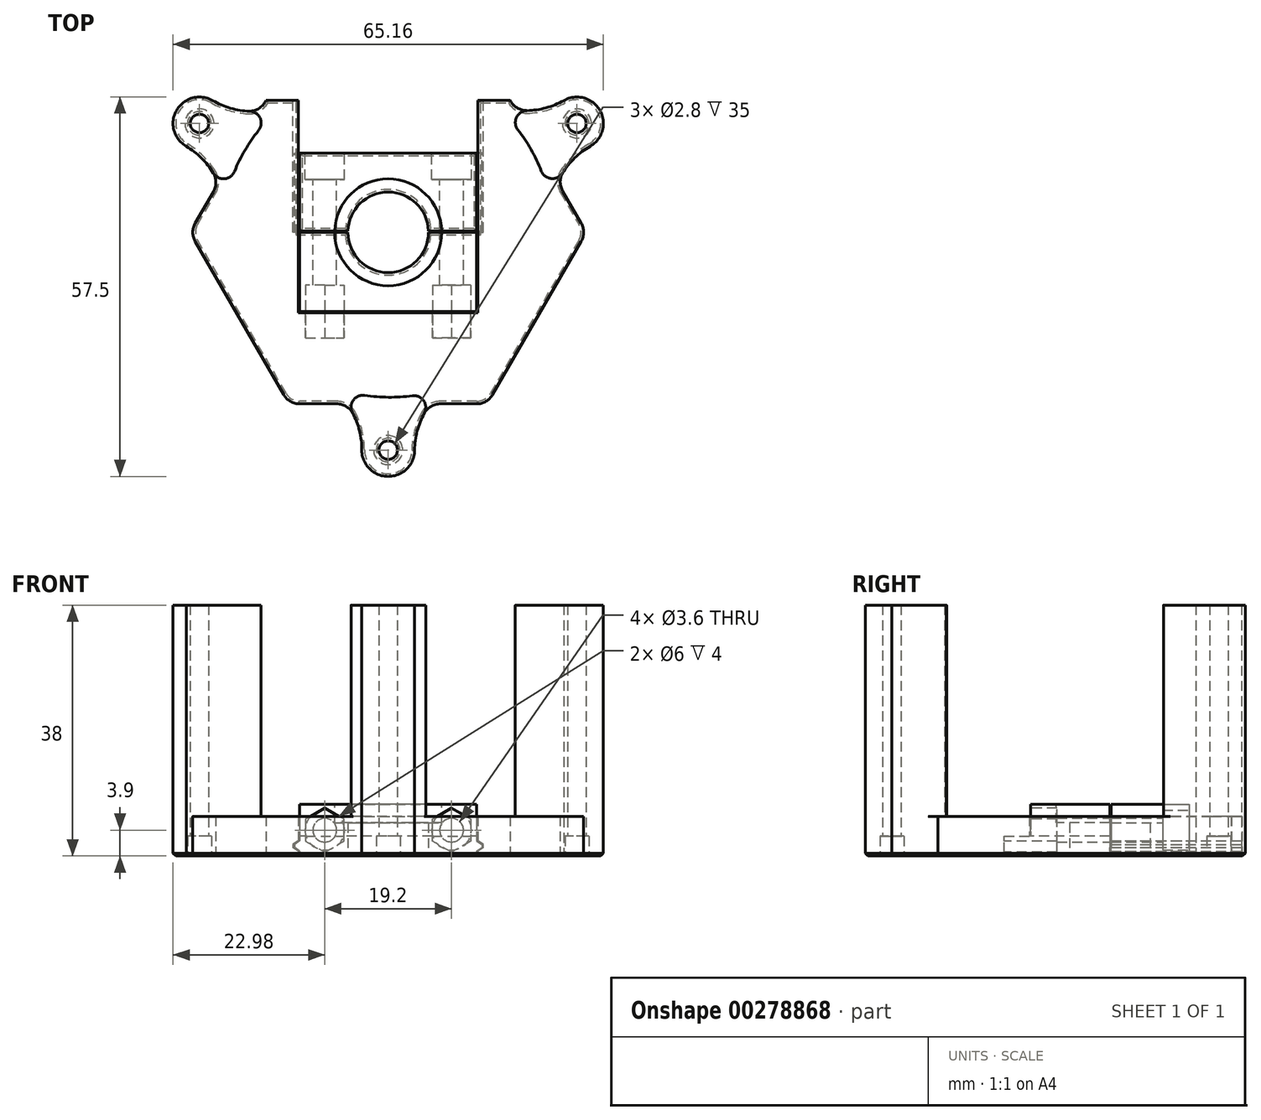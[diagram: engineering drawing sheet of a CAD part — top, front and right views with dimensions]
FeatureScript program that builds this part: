
annotation { "Feature Type Name" : "Feature", "Feature Type Description" : "" }
export const myFeature = defineFeature(function(context is Context, id is Id, definition is map)
    precondition{}
    {
        {
            var Q0;
            Q0=qCreatedBy(makeId("Top.planeOp"),FACE);
            var sketch = newSketch(context, id + "F0", { "sketchPlane" : qUnion([Q0])});
            skArc(sketch, "E0", {"start": v(-6.1, 0) * mm, "mid": v(0, -6.1) * mm, "end": v(6.1, 0) * mm});
            skLineSegment(sketch, "E1.bottom", {"start": v(13.4, -12) * mm, "end": v(-13.4, -12) * mm});
            skLineSegment(sketch, "E1.top", {"start": v(13.4, 12) * mm, "end": v(-13.4, 12) * mm});
            skLineSegment(sketch, "E1.left", {"start": v(13.4, -12) * mm, "end": v(13.4, 0) * mm});
            skLineSegment(sketch, "E1.right", {"start": v(-13.4, -12) * mm, "end": v(-13.4, 0) * mm});
            skLineSegment(sketch, "E2", {"start": v(-13.4, 0) * mm, "end": v(-6.1, 0) * mm});
            skLineSegment(sketch, "E3", {"start": v(-13.4, 0.2) * mm, "end": v(-6.1, 0.2) * mm});
            skLineSegment(sketch, "E4.trimOffspring", {"start": v(-13.4, 0.2) * mm, "end": v(-13.4, 12) * mm});
            skArc(sketch, "E5.trimOffspring", {"start": v(6.1, 0.2) * mm, "mid": v(0, 6.1) * mm, "end": v(-6.1, 0.2) * mm});
            skLineSegment(sketch, "E6.trimOffspring", {"start": v(13.4, 0.2) * mm, "end": v(13.4, 12) * mm});
            skLineSegment(sketch, "E7.trimOffspring", {"start": v(6.1, 0.2) * mm, "end": v(13.4, 0.2) * mm});
            skLineSegment(sketch, "E8.trimOffspring", {"start": v(6.1, 0) * mm, "end": v(13.4, 0) * mm});
            skSolve(sketch);
        }
        {
            var Q0;
            Q0 = qSketchRegion(id + "F0", true);
            extrude(context, id + "F1", {"entities" : qUnion([Q0]), "depth" : 7.8 * mm, "offsetDistance" : 25 * mm});
        }
        {
            var Q0;
            Q0=qCreatedBy(makeId("Top.planeOp"),FACE);
            var sketch = newSketch(context, id + "F2", { "sketchPlane" : qUnion([Q0])});
            skCircle(sketch, "E9.cCircle", {"center": v(0, 0) * mm, "radius": 26 * mm, "construction": true});
            skLineSegment(sketch, "E9.1", {"start": v(15.01, 26) * mm, "end": v(30.02, 0) * mm});
            skLineSegment(sketch, "E9.2", {"start": v(30.02, 0) * mm, "end": v(15.01, -26) * mm});
            skLineSegment(sketch, "E9.3", {"start": v(15.01, -26) * mm, "end": v(-15.01, -26) * mm});
            skLineSegment(sketch, "E9.4", {"start": v(-15.01, -26) * mm, "end": v(-30.02, 0) * mm});
            skLineSegment(sketch, "E9.5", {"start": v(-30.02, 0) * mm, "end": v(-15.01, 26) * mm});
            skPoint(sketch, "E9.0.midPoint", {"position": v(0, 26) * mm});
            skLineSegment(sketch, "E10", {"start": v(13.6, 0) * mm, "end": v(13.6, 20) * mm});
            skLineSegment(sketch, "E11", {"start": v(13.6, 20) * mm, "end": v(18.48, 20) * mm});
            skLineSegment(sketch, "E12", {"start": v(13.6, 0) * mm, "end": v(13.4, 0) * mm});
            skLineSegment(sketch, "E13", {"start": v(13.4, 0) * mm, "end": v(13.4, -12) * mm});
            skLineSegment(sketch, "E14", {"start": v(13.4, -12) * mm, "end": v(0, -12) * mm});
            skLineSegment(sketch, "E15.MirrorCS", {"start": v(-13.6, 20) * mm, "end": v(-18.48, 20) * mm});
            skLineSegment(sketch, "E16.MirrorCS", {"start": v(-13.6, 0) * mm, "end": v(-13.6, 20) * mm});
            skLineSegment(sketch, "E17.MirrorCS", {"start": v(-13.6, 0) * mm, "end": v(-13.4, 0) * mm});
            skLineSegment(sketch, "E18.MirrorCS", {"start": v(-13.4, 0) * mm, "end": v(-13.4, -12) * mm});
            skLineSegment(sketch, "E19.MirrorCS", {"start": v(-13.4, -12) * mm, "end": v(0, -12) * mm});
            skSolve(sketch);
        }
        {
            var Q0;
            Q0 = qSketchRegion(id + "F2", true);
            extrude(context, id + "F3", {"entities" : qUnion([Q0]), "operationType" : NewBodyOperationType.ADD, "depth" : 3 * mm, "offsetDistance" : 25 * mm});
        }
        {
            var Q0;
            Q0=makeQuery(id+"F3.opExtrude","SWEPT_FACE",FACE,{"disambiguationData":[OSD([sQuery(id+"F2.wireOp",EDGE,"E15.MirrorCS")])]});
            var sketch = newSketch(context, id + "F4", { "sketchPlane" : qUnion([Q0])});
            skLineSegment(sketch, "E20", {"start": v(14.4, 1.5) * mm, "end": v(13.6, 1.5) * mm});
            skLineSegment(sketch, "E21", {"start": v(14.4, 1.5) * mm, "end": v(14.4, 1.7) * mm});
            skLineSegment(sketch, "E22", {"start": v(14.4, 1.7) * mm, "end": v(13.6, 2.3) * mm});
            skLineSegment(sketch, "E23", {"start": v(13.6, 2.3) * mm, "end": v(13.6, 1.5) * mm});
            skLineSegment(sketch, "E24.MirrorCS", {"start": v(13.6, 0.7) * mm, "end": v(13.6, 1.5) * mm});
            skLineSegment(sketch, "E25.MirrorCS", {"start": v(14.4, 1.3) * mm, "end": v(13.6, 0.7) * mm});
            skLineSegment(sketch, "E26.MirrorCS", {"start": v(14.4, 1.5) * mm, "end": v(14.4, 1.3) * mm});
            skLineSegment(sketch, "E27.MirrorCS", {"start": v(-14.4, 1.5) * mm, "end": v(-14.4, 1.7) * mm});
            skLineSegment(sketch, "E28.MirrorCS", {"start": v(-14.4, 1.5) * mm, "end": v(-14.4, 1.3) * mm});
            skLineSegment(sketch, "E29.MirrorCS", {"start": v(-13.6, 2.3) * mm, "end": v(-13.6, 1.5) * mm});
            skLineSegment(sketch, "E30.MirrorCS", {"start": v(-14.4, 1.5) * mm, "end": v(-13.6, 1.5) * mm});
            skLineSegment(sketch, "E31.MirrorCS", {"start": v(-14.4, 1.7) * mm, "end": v(-13.6, 2.3) * mm});
            skLineSegment(sketch, "E32.MirrorCS", {"start": v(-13.6, 0.7) * mm, "end": v(-13.6, 1.5) * mm});
            skLineSegment(sketch, "E33.MirrorCS", {"start": v(-14.4, 1.3) * mm, "end": v(-13.6, 0.7) * mm});
            skSolve(sketch);
        }
        {
            var Q0;
            Q0 = qSketchRegion(id + "F4", true);
            var Q1;
            Q1=makeQuery(id+"F3.boolean.opBoolean","MERGE",FACE,{"derivedFrom":[makeQuery(id+"F1.opExtrude","SWEPT_FACE",FACE,{"disambiguationData":[OSD([sQuery(id+"F0.wireOp",EDGE,"E2")])]}),makeQuery(id+"F3.opExtrude","SWEPT_FACE",FACE,{"disambiguationData":[OSD([sQuery(id+"F2.wireOp",EDGE,"E17.MirrorCS")])]})]});
            extrude(context, id + "F5", {"entities" : qUnion([Q0]), "operationType" : NewBodyOperationType.REMOVE, "endBound" : BoundingType.UP_TO_SURFACE, "oppositeDirection" : true, "depth" : 25 * mm, "endBoundEntityFace" : qUnion([Q1]), "offsetDistance" : 25 * mm});
        }
        {
            var Q0;
            Q0=makeQuery(id+"F1.opExtrude","SWEPT_FACE",FACE,{"disambiguationData":[OSD([sQuery(id+"F0.wireOp",EDGE,"E1.top")])]});
            var sketch = newSketch(context, id + "F6", { "sketchPlane" : qUnion([Q0])});
            skCircle(sketch, "E34", {"center": v(-9.6, 3.9) * mm, "radius": 1.8 * mm});
            skCircle(sketch, "E35.MirrorC", {"center": v(9.6, 3.9) * mm, "radius": 1.8 * mm});
            skPoint(sketch, "E36", {"position": v(-13.4, 3.9) * mm});
            skSolve(sketch);
        }
        {
            var Q0;
            Q0 = qSketchRegion(id + "F6", true);
            var Q1;
            Q1=makeQuery(id+"F1.opExtrude","SWEPT_FACE",FACE,{"disambiguationData":[OSD([sQuery(id+"F0.wireOp",EDGE,"E1.bottom")])]});
            extrude(context, id + "F7", {"entities" : qUnion([Q0]), "operationType" : NewBodyOperationType.REMOVE, "endBound" : BoundingType.UP_TO_SURFACE, "oppositeDirection" : true, "depth" : 25 * mm, "endBoundEntityFace" : qUnion([Q1]), "offsetDistance" : 25 * mm});
        }
        {
            var Q0;
            Q0=makeQuery(id+"F1.opExtrude","SWEPT_FACE",FACE,{"disambiguationData":[OSD([sQuery(id+"F0.wireOp",EDGE,"E1.top")])]});
            var sketch = newSketch(context, id + "F8", { "sketchPlane" : qUnion([Q0])});
            skCircle(sketch, "E37", {"center": v(9.6, 3.9) * mm, "radius": 3 * mm});
            skCircle(sketch, "E38.MirrorC", {"center": v(-9.6, 3.9) * mm, "radius": 3 * mm});
            skSolve(sketch);
        }
        {
            var Q0;
            Q0 = qSketchRegion(id + "F8", true);
            extrude(context, id + "F9", {"entities" : qUnion([Q0]), "operationType" : NewBodyOperationType.REMOVE, "oppositeDirection" : true, "depth" : 4 * mm, "offsetDistance" : 25 * mm});
        }
        {
            var Q0;
            Q0=makeQuery(id+"F1.opExtrude","SWEPT_FACE",FACE,{"disambiguationData":[OSD([sQuery(id+"F0.wireOp",EDGE,"E1.bottom")])]});
            var sketch = newSketch(context, id + "F10", { "sketchPlane" : qUnion([Q0])});
            skCircle(sketch, "E39.cCircle", {"center": v(9.6, 3.9) * mm, "radius": 2.9 * mm, "construction": true});
            skLineSegment(sketch, "E39.0", {"start": v(12.5, 5.57) * mm, "end": v(12.5, 2.23) * mm});
            skLineSegment(sketch, "E39.1", {"start": v(12.5, 2.23) * mm, "end": v(9.6, 0.55) * mm});
            skLineSegment(sketch, "E39.2", {"start": v(9.6, 0.55) * mm, "end": v(6.7, 2.23) * mm});
            skLineSegment(sketch, "E39.3", {"start": v(6.7, 2.23) * mm, "end": v(6.7, 5.57) * mm});
            skLineSegment(sketch, "E39.4", {"start": v(6.7, 5.57) * mm, "end": v(9.6, 7.25) * mm});
            skLineSegment(sketch, "E39.5", {"start": v(9.6, 7.25) * mm, "end": v(12.5, 5.57) * mm});
            skPoint(sketch, "E39.0.midPoint", {"position": v(12.5, 3.9) * mm});
            skLineSegment(sketch, "E40.MirrorCS", {"start": v(-6.7, 5.57) * mm, "end": v(-9.6, 7.25) * mm});
            skPoint(sketch, "E41.MirrorP", {"position": v(-12.5, 3.9) * mm});
            skLineSegment(sketch, "E42.MirrorCS", {"start": v(-9.6, 7.25) * mm, "end": v(-12.5, 5.57) * mm});
            skCircle(sketch, "E43.MirrorC", {"center": v(-9.6, 3.9) * mm, "radius": 2.9 * mm, "construction": true});
            skLineSegment(sketch, "E44.MirrorCS", {"start": v(-9.6, 0.55) * mm, "end": v(-6.7, 2.23) * mm});
            skLineSegment(sketch, "E45.MirrorCS", {"start": v(-12.5, 5.57) * mm, "end": v(-12.5, 2.23) * mm});
            skLineSegment(sketch, "E46.MirrorCS", {"start": v(-12.5, 2.23) * mm, "end": v(-9.6, 0.55) * mm});
            skLineSegment(sketch, "E47.MirrorCS", {"start": v(-6.7, 2.23) * mm, "end": v(-6.7, 5.57) * mm});
            skSolve(sketch);
        }
        {
            var Q0;
            Q0 = qSketchRegion(id + "F10", true);
            extrude(context, id + "F11", {"entities" : qUnion([Q0]), "operationType" : NewBodyOperationType.REMOVE, "endBound" : BoundingType.SYMMETRIC, "oppositeDirection" : true, "depth" : 8 * mm, "offsetDistance" : 25 * mm});
        }
        {
            var Q0;
            Q0=makeQuery(id+"F1.opExtrude","CAP_FACE",FACE,{"disambiguationData":[OSD([sQuery(id+"F0.wireOp",EDGE,"E0"),sQuery(id+"F0.wireOp",EDGE,"E1.bottom"),sQuery(id+"F0.wireOp",EDGE,"E1.left"),sQuery(id+"F0.wireOp",EDGE,"E1.right"),sQuery(id+"F0.wireOp",EDGE,"E2"),sQuery(id+"F0.wireOp",EDGE,"E8.trimOffspring")])],"isStart":false});
            var sketch = newSketch(context, id + "F12", { "sketchPlane" : qUnion([Q0])});
            skCircle(sketch, "E48", {"center": v(0, 0) * mm, "radius": 8.1 * mm});
            skSolve(sketch);
        }
        {
            var Q0;
            Q0 = qSketchRegion(id + "F12", true);
            extrude(context, id + "F13", {"entities" : qUnion([Q0]), "operationType" : NewBodyOperationType.REMOVE, "oppositeDirection" : true, "depth" : 2.8 * mm, "offsetDistance" : 25 * mm});
        }
        {
            var Q0;
            Q0=qCreatedBy(makeId("Top.planeOp"),FACE);
            var sketch = newSketch(context, id + "F14", { "sketchPlane" : qUnion([Q0])});
            skArc(sketch, "E49", {"start": v(-9, -23.23) * mm, "mid": v(-0.02, -25) * mm, "end": v(9, -23.41) * mm});
            skCircle(sketch, "E50", {"center": v(0, -33) * mm, "radius": 4 * mm});
            skArc(sketch, "E51", {"start": v(9, -23.41) * mm, "mid": v(5.36, -27.61) * mm, "end": v(4, -33) * mm});
            skArc(sketch, "E52.MirrorCS", {"start": v(-9, -23.23) * mm, "mid": v(-5.32, -27.5) * mm, "end": v(-4, -33) * mm});
            skCircle(sketch, "E53", {"center": v(0, -33) * mm, "radius": 1.8 * mm});
            skCircle(sketch, "E54.1.0", {"center": v(28.58, 16.5) * mm, "radius": 1.8 * mm});
            skArc(sketch, "E54.1.1", {"start": v(15.78, 19.5) * mm, "mid": v(21.23, 18.45) * mm, "end": v(26.58, 19.96) * mm});
            skArc(sketch, "E54.1.2", {"start": v(24.62, 3.82) * mm, "mid": v(26.48, 9.15) * mm, "end": v(30.58, 13.04) * mm});
            skCircle(sketch, "E54.1.3", {"center": v(28.58, 16.5) * mm, "radius": 4 * mm});
            skArc(sketch, "E54.1.4", {"start": v(24.62, 3.82) * mm, "mid": v(21.66, 12.48) * mm, "end": v(15.78, 19.5) * mm});
            skCircle(sketch, "E54.2.0", {"center": v(-28.58, 16.5) * mm, "radius": 1.8 * mm});
            skArc(sketch, "E54.2.1", {"start": v(-24.78, 3.91) * mm, "mid": v(-26.6, 9.16) * mm, "end": v(-30.58, 13.04) * mm});
            skArc(sketch, "E54.2.2", {"start": v(-15.62, 19.4) * mm, "mid": v(-21.17, 18.36) * mm, "end": v(-26.58, 19.96) * mm});
            skCircle(sketch, "E54.2.3", {"center": v(-28.58, 16.5) * mm, "radius": 4 * mm});
            skArc(sketch, "E54.2.4", {"start": v(-15.62, 19.4) * mm, "mid": v(-21.64, 12.51) * mm, "end": v(-24.78, 3.91) * mm});
            skPoint(sketch, "E54.center", {"position": v(0, 0) * mm});
            skSolve(sketch);
        }
        {
            var Q0;
            Q0 = qSketchRegion(id + "F14", true);
            extrude(context, id + "F15", {"entities" : qUnion([Q0]), "operationType" : NewBodyOperationType.ADD, "depth" : 3 * mm, "offsetDistance" : 25 * mm});
        }
        {
            var Q0;
            Q0=makeQuery(id+"F1.opExtrude","SWEPT_FACE",FACE,{"disambiguationData":[OSD([sQuery(id+"F0.wireOp",EDGE,"E1.top")])]});
            var sketch = newSketch(context, id + "F16", { "sketchPlane" : qUnion([Q0])});
            skPoint(sketch, "E55", {"position": v(14.58, 1.5) * mm});
            skLineSegment(sketch, "E56", {"start": v(13.4, 1.5) * mm, "end": v(14.2, 1.5) * mm});
            skLineSegment(sketch, "E57", {"start": v(14.2, 1.5) * mm, "end": v(14.2, 1.7) * mm});
            skLineSegment(sketch, "E58", {"start": v(14.2, 1.7) * mm, "end": v(13.4, 2.3) * mm});
            skLineSegment(sketch, "E59", {"start": v(13.4, 2.3) * mm, "end": v(13.4, 1.5) * mm});
            skLineSegment(sketch, "E60.MirrorCS", {"start": v(13.4, 0.7) * mm, "end": v(13.4, 1.5) * mm});
            skLineSegment(sketch, "E61.MirrorCS", {"start": v(14.2, 1.3) * mm, "end": v(13.4, 0.7) * mm});
            skLineSegment(sketch, "E62.MirrorCS", {"start": v(14.2, 1.5) * mm, "end": v(14.2, 1.3) * mm});
            skLineSegment(sketch, "E63.MirrorCS", {"start": v(-14.2, 1.5) * mm, "end": v(-14.2, 1.7) * mm});
            skLineSegment(sketch, "E64.MirrorCS", {"start": v(-14.2, 1.5) * mm, "end": v(-14.2, 1.3) * mm});
            skLineSegment(sketch, "E65.MirrorCS", {"start": v(-13.4, 1.5) * mm, "end": v(-14.2, 1.5) * mm});
            skLineSegment(sketch, "E66.MirrorCS", {"start": v(-13.4, 0.7) * mm, "end": v(-13.4, 1.5) * mm});
            skLineSegment(sketch, "E67.MirrorCS", {"start": v(-14.2, 1.3) * mm, "end": v(-13.4, 0.7) * mm});
            skLineSegment(sketch, "E68.MirrorCS", {"start": v(-13.4, 2.3) * mm, "end": v(-13.4, 1.5) * mm});
            skPoint(sketch, "E69.MirrorP", {"position": v(-14.58, 1.5) * mm});
            skLineSegment(sketch, "E70.MirrorCS", {"start": v(-14.2, 1.7) * mm, "end": v(-13.4, 2.3) * mm});
            skSolve(sketch);
        }
        {
            var Q0;
            Q0 = qSketchRegion(id + "F16", true);
            var Q1;
            Q1=makeQuery(id+"F1.opExtrude","SWEPT_FACE",FACE,{"disambiguationData":[OSD([sQuery(id+"F0.wireOp",EDGE,"E7.trimOffspring")])]});
            extrude(context, id + "F17", {"entities" : qUnion([Q0]), "operationType" : NewBodyOperationType.ADD, "endBound" : BoundingType.UP_TO_SURFACE, "oppositeDirection" : true, "depth" : 25 * mm, "endBoundEntityFace" : qUnion([Q1]), "offsetDistance" : 25 * mm});
        }
        {
            var Q0;
            Q0=makeQuery(id+"F15.boolean.opBoolean","INTERSECT",EDGE,{"derivedFrom":[makeQuery(id+"F3.opExtrude","SWEPT_FACE",FACE,{"disambiguationData":[OSD([sQuery(id+"F2.wireOp",EDGE,"E9.1")])]}),makeQuery(id+"F15.opExtrude","SWEPT_FACE",FACE,{"disambiguationData":[OSD([sQuery(id+"F14.wireOp",EDGE,"E54.1.1")])]})]});
            var Q1;
            Q1=makeQuery(id+"F15.boolean.opBoolean","INTERSECT",EDGE,{"derivedFrom":[makeQuery(id+"F3.opExtrude","SWEPT_FACE",FACE,{"disambiguationData":[OSD([sQuery(id+"F2.wireOp",EDGE,"E9.5")])]}),makeQuery(id+"F15.opExtrude","SWEPT_FACE",FACE,{"disambiguationData":[OSD([sQuery(id+"F14.wireOp",EDGE,"E54.2.2")])]})]});
            var Q2;
            Q2=makeQuery(id+"F15.boolean.opBoolean","INTERSECT",EDGE,{"derivedFrom":[makeQuery(id+"F3.opExtrude","SWEPT_FACE",FACE,{"disambiguationData":[OSD([sQuery(id+"F2.wireOp",EDGE,"E9.5")])]}),makeQuery(id+"F15.opExtrude","SWEPT_FACE",FACE,{"disambiguationData":[OSD([sQuery(id+"F14.wireOp",EDGE,"E54.2.1")])]})]});
            var Q3;
            Q3=makeQuery(id+"F3.opExtrude","SWEPT_EDGE",EDGE,{"disambiguationData":[OSD([sQuery(id+"F2.wireOp",EDGE,"E9.4"),sQuery(id+"F2.wireOp",EDGE,"E9.5")])]});
            var Q4;
            Q4=makeQuery(id+"F3.opExtrude","SWEPT_EDGE",EDGE,{"disambiguationData":[OSD([sQuery(id+"F2.wireOp",EDGE,"E9.3"),sQuery(id+"F2.wireOp",EDGE,"E9.4")])]});
            var Q5;
            Q5=makeQuery(id+"F15.boolean.opBoolean","INTERSECT",EDGE,{"derivedFrom":[makeQuery(id+"F3.opExtrude","SWEPT_FACE",FACE,{"disambiguationData":[OSD([sQuery(id+"F2.wireOp",EDGE,"E9.3")])]}),makeQuery(id+"F15.opExtrude","SWEPT_FACE",FACE,{"disambiguationData":[OSD([sQuery(id+"F14.wireOp",EDGE,"E52.MirrorCS")])]})]});
            var Q6;
            Q6=makeQuery(id+"F15.boolean.opBoolean","INTERSECT",EDGE,{"derivedFrom":[makeQuery(id+"F3.opExtrude","SWEPT_FACE",FACE,{"disambiguationData":[OSD([sQuery(id+"F2.wireOp",EDGE,"E9.3")])]}),makeQuery(id+"F15.opExtrude","SWEPT_FACE",FACE,{"disambiguationData":[OSD([sQuery(id+"F14.wireOp",EDGE,"E51")])]})]});
            var Q7;
            Q7=makeQuery(id+"F3.opExtrude","SWEPT_EDGE",EDGE,{"disambiguationData":[OSD([sQuery(id+"F2.wireOp",EDGE,"E9.2"),sQuery(id+"F2.wireOp",EDGE,"E9.3")])]});
            var Q8;
            Q8=makeQuery(id+"F3.opExtrude","SWEPT_EDGE",EDGE,{"disambiguationData":[OSD([sQuery(id+"F2.wireOp",EDGE,"E9.1"),sQuery(id+"F2.wireOp",EDGE,"E9.2")])]});
            var Q9;
            Q9=makeQuery(id+"F15.boolean.opBoolean","INTERSECT",EDGE,{"derivedFrom":[makeQuery(id+"F3.opExtrude","SWEPT_FACE",FACE,{"disambiguationData":[OSD([sQuery(id+"F2.wireOp",EDGE,"E9.1")])]}),makeQuery(id+"F15.opExtrude","SWEPT_FACE",FACE,{"disambiguationData":[OSD([sQuery(id+"F14.wireOp",EDGE,"E54.1.2")])]})]});
            fillet(context, id + "F18", {"entities" : qUnion([Q0, Q1, Q2, Q3, Q4, Q5, Q6, Q7, Q8, Q9]), "tangentPropagation" : true, "radius" : 2.8 * mm, "defaultsChanged" : false, "vertexSettings" : [], "allowEdgeOverflow" : false});
        }
        {
            var Q0;
            Q0=makeQuery(id+"F1.opExtrude","CAP_FACE",FACE,{"disambiguationData":[OSD([sQuery(id+"F0.wireOp",EDGE,"E0"),sQuery(id+"F0.wireOp",EDGE,"E1.bottom"),sQuery(id+"F0.wireOp",EDGE,"E1.left"),sQuery(id+"F0.wireOp",EDGE,"E1.right"),sQuery(id+"F0.wireOp",EDGE,"E2"),sQuery(id+"F0.wireOp",EDGE,"E8.trimOffspring")])],"isStart":true});
            var Q1;
            Q1=makeQuery(id+"F1.opExtrude","CAP_FACE",FACE,{"disambiguationData":[OSD([sQuery(id+"F0.wireOp",EDGE,"E1.top"),sQuery(id+"F0.wireOp",EDGE,"E3"),sQuery(id+"F0.wireOp",EDGE,"E4.trimOffspring"),sQuery(id+"F0.wireOp",EDGE,"E5.trimOffspring"),sQuery(id+"F0.wireOp",EDGE,"E6.trimOffspring"),sQuery(id+"F0.wireOp",EDGE,"E7.trimOffspring")])],"isStart":true});
            chamfer(context, id + "F19", {"entities" : qUnion([Q0, Q1]), "width" : .4 * mm, "tangentPropagation" : true});
        }
        {
            var Q0;
            Q0=makeQuery(id+"F15.boolean.opBoolean","MERGE",FACE,{"derivedFrom":[makeQuery(id+"F3.opExtrude","CAP_FACE",FACE,{"disambiguationData":[OSD([sQuery(id+"F2.wireOp",EDGE,"E9.1"),sQuery(id+"F2.wireOp",EDGE,"E9.2"),sQuery(id+"F2.wireOp",EDGE,"E9.3"),sQuery(id+"F2.wireOp",EDGE,"E9.4"),sQuery(id+"F2.wireOp",EDGE,"E9.5"),sQuery(id+"F2.wireOp",EDGE,"E10"),sQuery(id+"F2.wireOp",EDGE,"E11"),sQuery(id+"F2.wireOp",EDGE,"E12"),sQuery(id+"F2.wireOp",EDGE,"E13"),sQuery(id+"F2.wireOp",EDGE,"E14"),sQuery(id+"F2.wireOp",EDGE,"E15.MirrorCS"),sQuery(id+"F2.wireOp",EDGE,"E16.MirrorCS"),sQuery(id+"F2.wireOp",EDGE,"E17.MirrorCS"),sQuery(id+"F2.wireOp",EDGE,"E18.MirrorCS"),sQuery(id+"F2.wireOp",EDGE,"E19.MirrorCS")])],"isStart":false}),makeQuery(id+"F15.opExtrude","CAP_FACE",FACE,{"disambiguationData":[OSD([sQuery(id+"F14.wireOp",EDGE,"E49"),sQuery(id+"F14.wireOp",EDGE,"E50"),sQuery(id+"F14.wireOp",EDGE,"E51"),sQuery(id+"F14.wireOp",EDGE,"E52.MirrorCS"),sQuery(id+"F14.wireOp",EDGE,"E53")])],"isStart":false}),makeQuery(id+"F15.opExtrude","CAP_FACE",FACE,{"disambiguationData":[OSD([sQuery(id+"F14.wireOp",EDGE,"E54.1.0"),sQuery(id+"F14.wireOp",EDGE,"E54.1.1"),sQuery(id+"F14.wireOp",EDGE,"E54.1.2"),sQuery(id+"F14.wireOp",EDGE,"E54.1.3"),sQuery(id+"F14.wireOp",EDGE,"E54.1.4")])],"isStart":false}),makeQuery(id+"F15.opExtrude","CAP_FACE",FACE,{"disambiguationData":[OSD([sQuery(id+"F14.wireOp",EDGE,"E54.2.0"),sQuery(id+"F14.wireOp",EDGE,"E54.2.1"),sQuery(id+"F14.wireOp",EDGE,"E54.2.2"),sQuery(id+"F14.wireOp",EDGE,"E54.2.3"),sQuery(id+"F14.wireOp",EDGE,"E54.2.4")])],"isStart":false})]});
            cPlane(context, id + "F20", {"entities" : qUnion([Q0]), "cplaneType" : CPlaneType.OFFSET, "offset" : 0 * mm, "width" : 150 * mm, "height" : 150 * mm});
        }
        {
            var Q0;
            Q0=qCreatedBy(id+"F20.planeOp",FACE);
            var sketch = newSketch(context, id + "F21", { "sketchPlane" : qUnion([Q0])});
            skCircle(sketch, "E71.cCircle", {"center": v(0, 0) * mm, "radius": 26 * mm, "construction": true});
            skLineSegment(sketch, "E71.1", {"start": v(15.01, 26) * mm, "end": v(30.02, 0) * mm});
            skLineSegment(sketch, "E71.2", {"start": v(30.02, 0) * mm, "end": v(15.01, -26) * mm});
            skLineSegment(sketch, "E71.3", {"start": v(15.01, -26) * mm, "end": v(-15.01, -26) * mm});
            skLineSegment(sketch, "E71.4", {"start": v(-15.01, -26) * mm, "end": v(-30.02, 0) * mm});
            skLineSegment(sketch, "E71.5", {"start": v(-30.02, 0) * mm, "end": v(-15.01, 26) * mm});
            skPoint(sketch, "E71.0.midPoint", {"position": v(0, 26) * mm});
            skLineSegment(sketch, "E72", {"start": v(18.48, 20) * mm, "end": v(13.6, 20) * mm});
            skLineSegment(sketch, "E73", {"start": v(13.6, 20) * mm, "end": v(13.6, -12.2) * mm});
            skLineSegment(sketch, "E74", {"start": v(13.6, -12.2) * mm, "end": v(0, -12.2) * mm});
            skLineSegment(sketch, "E75.MirrorCS", {"start": v(-18.48, 20) * mm, "end": v(-13.6, 20) * mm});
            skLineSegment(sketch, "E76.MirrorCS", {"start": v(-13.6, 20) * mm, "end": v(-13.6, -12.2) * mm});
            skLineSegment(sketch, "E77.MirrorCS", {"start": v(-13.6, -12.2) * mm, "end": v(0, -12.2) * mm});
            skSolve(sketch);
        }
        {
            var Q0;
            Q0 = qSketchRegion(id + "F21", true);
            extrude(context, id + "F22", {"entities" : qUnion([Q0]), "depth" : 3 * mm, "offsetDistance" : 25 * mm});
        }
        {
            var Q0;
            Q0=qCreatedBy(id+"F20.planeOp",FACE);
            var sketch = newSketch(context, id + "F23", { "sketchPlane" : qUnion([Q0])});
            skArc(sketch, "E78", {"start": v(-9, -23.23) * mm, "mid": v(-0.02, -25) * mm, "end": v(9, -23.41) * mm});
            skCircle(sketch, "E79", {"center": v(0, -33) * mm, "radius": 4 * mm});
            skArc(sketch, "E80", {"start": v(9, -23.41) * mm, "mid": v(5.36, -27.61) * mm, "end": v(4, -33) * mm});
            skArc(sketch, "E81.MirrorCS", {"start": v(-9, -23.23) * mm, "mid": v(-5.32, -27.5) * mm, "end": v(-4, -33) * mm});
            skCircle(sketch, "E82", {"center": v(0, -33) * mm, "radius": 1.4 * mm});
            skArc(sketch, "E83.1.0", {"start": v(15.78, 19.5) * mm, "mid": v(21.23, 18.45) * mm, "end": v(26.58, 19.96) * mm});
            skArc(sketch, "E83.1.1", {"start": v(24.62, 3.82) * mm, "mid": v(26.48, 9.15) * mm, "end": v(30.58, 13.04) * mm});
            skArc(sketch, "E83.1.2", {"start": v(24.62, 3.82) * mm, "mid": v(21.66, 12.48) * mm, "end": v(15.78, 19.5) * mm});
            skCircle(sketch, "E83.1.3", {"center": v(28.58, 16.5) * mm, "radius": 1.4 * mm});
            skCircle(sketch, "E83.1.4", {"center": v(28.58, 16.5) * mm, "radius": 4 * mm});
            skArc(sketch, "E83.2.0", {"start": v(-24.78, 3.91) * mm, "mid": v(-26.6, 9.16) * mm, "end": v(-30.58, 13.04) * mm});
            skArc(sketch, "E83.2.1", {"start": v(-15.62, 19.4) * mm, "mid": v(-21.17, 18.36) * mm, "end": v(-26.58, 19.96) * mm});
            skArc(sketch, "E83.2.2", {"start": v(-15.62, 19.4) * mm, "mid": v(-21.64, 12.51) * mm, "end": v(-24.78, 3.91) * mm});
            skCircle(sketch, "E83.2.3", {"center": v(-28.58, 16.5) * mm, "radius": 1.4 * mm});
            skCircle(sketch, "E83.2.4", {"center": v(-28.58, 16.5) * mm, "radius": 4 * mm});
            skPoint(sketch, "E83.center", {"position": v(0, 0) * mm});
            skSolve(sketch);
        }
        {
            var Q0;
            Q0 = qSketchRegion(id + "F23", true);
            extrude(context, id + "F24", {"entities" : qUnion([Q0]), "operationType" : NewBodyOperationType.ADD, "depth" : 35 * mm, "offsetDistance" : 25 * mm});
        }
        {
            var Q0;
            Q0=makeQuery(id+"F24.boolean.opBoolean","INTERSECT",EDGE,{"derivedFrom":[makeQuery(id+"F22.opExtrude","SWEPT_FACE",FACE,{"disambiguationData":[OSD([sQuery(id+"F21.wireOp",EDGE,"E71.5")])]}),makeQuery(id+"F24.opExtrude","SWEPT_FACE",FACE,{"disambiguationData":[OSD([sQuery(id+"F23.wireOp",EDGE,"E83.2.0")])]})]});
            var Q1;
            Q1=makeQuery(id+"F22.opExtrude","SWEPT_EDGE",EDGE,{"disambiguationData":[OSD([sQuery(id+"F21.wireOp",EDGE,"E71.4"),sQuery(id+"F21.wireOp",EDGE,"E71.5")])]});
            var Q2;
            Q2=makeQuery(id+"F22.opExtrude","SWEPT_EDGE",EDGE,{"disambiguationData":[OSD([sQuery(id+"F21.wireOp",EDGE,"E71.3"),sQuery(id+"F21.wireOp",EDGE,"E71.4")])]});
            var Q3;
            Q3=makeQuery(id+"F24.boolean.opBoolean","INTERSECT",EDGE,{"derivedFrom":[makeQuery(id+"F22.opExtrude","SWEPT_FACE",FACE,{"disambiguationData":[OSD([sQuery(id+"F21.wireOp",EDGE,"E71.3")])]}),makeQuery(id+"F24.opExtrude","SWEPT_FACE",FACE,{"disambiguationData":[OSD([sQuery(id+"F23.wireOp",EDGE,"E81.MirrorCS")])]})]});
            var Q4;
            Q4=makeQuery(id+"F24.boolean.opBoolean","INTERSECT",EDGE,{"derivedFrom":[makeQuery(id+"F22.opExtrude","SWEPT_FACE",FACE,{"disambiguationData":[OSD([sQuery(id+"F21.wireOp",EDGE,"E71.3")])]}),makeQuery(id+"F24.opExtrude","SWEPT_FACE",FACE,{"disambiguationData":[OSD([sQuery(id+"F23.wireOp",EDGE,"E80")])]})]});
            var Q5;
            Q5=makeQuery(id+"F22.opExtrude","SWEPT_EDGE",EDGE,{"disambiguationData":[OSD([sQuery(id+"F21.wireOp",EDGE,"E71.2"),sQuery(id+"F21.wireOp",EDGE,"E71.3")])]});
            var Q6;
            Q6=makeQuery(id+"F22.opExtrude","SWEPT_EDGE",EDGE,{"disambiguationData":[OSD([sQuery(id+"F21.wireOp",EDGE,"E71.1"),sQuery(id+"F21.wireOp",EDGE,"E71.2")])]});
            var Q7;
            Q7=makeQuery(id+"F24.boolean.opBoolean","INTERSECT",EDGE,{"derivedFrom":[makeQuery(id+"F22.opExtrude","SWEPT_FACE",FACE,{"disambiguationData":[OSD([sQuery(id+"F21.wireOp",EDGE,"E71.1")])]}),makeQuery(id+"F24.opExtrude","SWEPT_FACE",FACE,{"disambiguationData":[OSD([sQuery(id+"F23.wireOp",EDGE,"E83.1.1")])]})]});
            var Q8;
            Q8=makeQuery(id+"F24.boolean.opBoolean","INTERSECT",EDGE,{"derivedFrom":[makeQuery(id+"F22.opExtrude","SWEPT_FACE",FACE,{"disambiguationData":[OSD([sQuery(id+"F21.wireOp",EDGE,"E71.1")])]}),makeQuery(id+"F24.opExtrude","SWEPT_FACE",FACE,{"disambiguationData":[OSD([sQuery(id+"F23.wireOp",EDGE,"E83.1.0")])]})]});
            var Q9;
            Q9=makeQuery(id+"F24.boolean.opBoolean","INTERSECT",EDGE,{"derivedFrom":[makeQuery(id+"F22.opExtrude","SWEPT_FACE",FACE,{"disambiguationData":[OSD([sQuery(id+"F21.wireOp",EDGE,"E71.5")])]}),makeQuery(id+"F24.opExtrude","SWEPT_FACE",FACE,{"disambiguationData":[OSD([sQuery(id+"F23.wireOp",EDGE,"E83.2.1")])]})]});
            fillet(context, id + "F25", {"entities" : qUnion([Q0, Q1, Q2, Q3, Q4, Q5, Q6, Q7, Q8, Q9]), "tangentPropagation" : true, "radius" : 2.8 * mm, "defaultsChanged" : false, "vertexSettings" : [], "allowEdgeOverflow" : false});
        }
        {
            var Q0;
            Q0=makeQuery(id+"F24.opExtrude","SWEPT_EDGE",EDGE,{"disambiguationData":[OSD([sQuery(id+"F23.wireOp",EDGE,"E83.1.0"),sQuery(id+"F23.wireOp",EDGE,"E83.1.2")])]});
            var Q1;
            Q1=makeQuery(id+"F24.opExtrude","SWEPT_EDGE",EDGE,{"disambiguationData":[OSD([sQuery(id+"F23.wireOp",EDGE,"E83.1.1"),sQuery(id+"F23.wireOp",EDGE,"E83.1.2")])]});
            var Q2;
            Q2=makeQuery(id+"F24.opExtrude","SWEPT_EDGE",EDGE,{"disambiguationData":[OSD([sQuery(id+"F23.wireOp",EDGE,"E83.2.1"),sQuery(id+"F23.wireOp",EDGE,"E83.2.2")])]});
            var Q3;
            Q3=makeQuery(id+"F24.opExtrude","SWEPT_EDGE",EDGE,{"disambiguationData":[OSD([sQuery(id+"F23.wireOp",EDGE,"E83.2.0"),sQuery(id+"F23.wireOp",EDGE,"E83.2.2")])]});
            var Q4;
            Q4=makeQuery(id+"F24.opExtrude","SWEPT_EDGE",EDGE,{"disambiguationData":[OSD([sQuery(id+"F23.wireOp",EDGE,"E78"),sQuery(id+"F23.wireOp",EDGE,"E81.MirrorCS")])]});
            var Q5;
            Q5=makeQuery(id+"F24.opExtrude","SWEPT_EDGE",EDGE,{"disambiguationData":[OSD([sQuery(id+"F23.wireOp",EDGE,"E78"),sQuery(id+"F23.wireOp",EDGE,"E80")])]});
            fillet(context, id + "F26", {"entities" : qUnion([Q0, Q1, Q2, Q3, Q4, Q5]), "tangentPropagation" : true, "radius" : 1.8 * mm, "defaultsChanged" : false, "vertexSettings" : [], "allowEdgeOverflow" : false});
        }
    });
